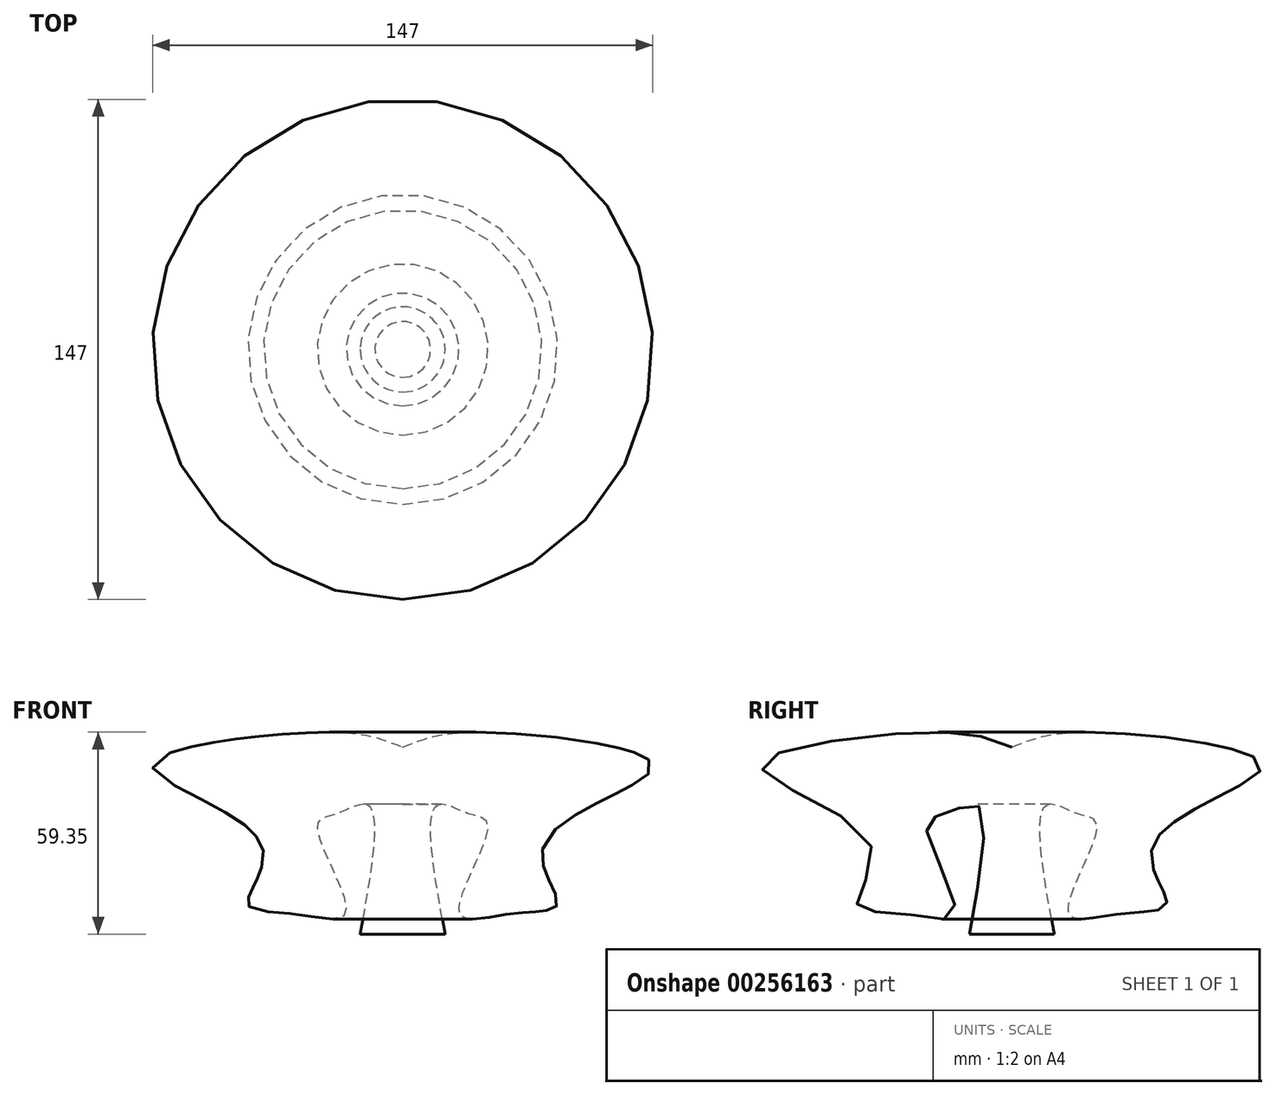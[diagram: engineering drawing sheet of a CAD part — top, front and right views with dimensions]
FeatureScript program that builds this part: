
annotation { "Feature Type Name" : "Feature", "Feature Type Description" : "" }
export const myFeature = defineFeature(function(context is Context, id is Id, definition is map)
    precondition{}
    {
        {
            var Q0;
            Q0=qCreatedBy(makeId("Right.planeOp"),FACE);
            var sketch = newSketch(context, id + "F0", { "sketchPlane" : qUnion([Q0])});
            skFitSpline(sketch, "E0", {"points": [v(0, 54.96) * mm, v(-25.15, 59.3) * mm, v(-73.49, 49.06) * mm, v(-41.63, 26.56) * mm, v(-45.53, 9) * mm, v(-31.87, 5.96) * mm, v(-16.7, 6.4) * mm, v(-25.15, 31.76) * mm, v(-19.13, 35.45) * mm, v(-9.54, 37.4) * mm, v(-12.5, 0) * mm], "startDerivative": vector(-239.66, 95.54) * mm, "endDerivative": vector(-40.53, -220.78) * mm});
            skLineSegment(sketch, "E1", {"start": v(-12.5, 0) * mm, "end": v(0, 0) * mm});
            skLineSegment(sketch, "E2", {"start": v(0, 0) * mm, "end": v(0, 54.96) * mm});
            skSolve(sketch);
        }
        {
            var Q0;
            Q0=makeQuery(id+"F0.imprint","IMPRINT",FACE,{"disambiguationData":[TD([[makeQuery(id+"F0.imprint","IMPRINT",EDGE,{"derivedFrom":sQuery(id+"F0.wireOp",EDGE,"E0")}),1.0]])]});
            var Q1;
            Q1=sQuery(id+"F0.wireOp",EDGE,"E2");
            revolve(context, id + "F1", {"entities" : qUnion([Q0]), "axis" : qUnion([Q1]), "revolveType" : RevolveType.FULL});
        }
    });
